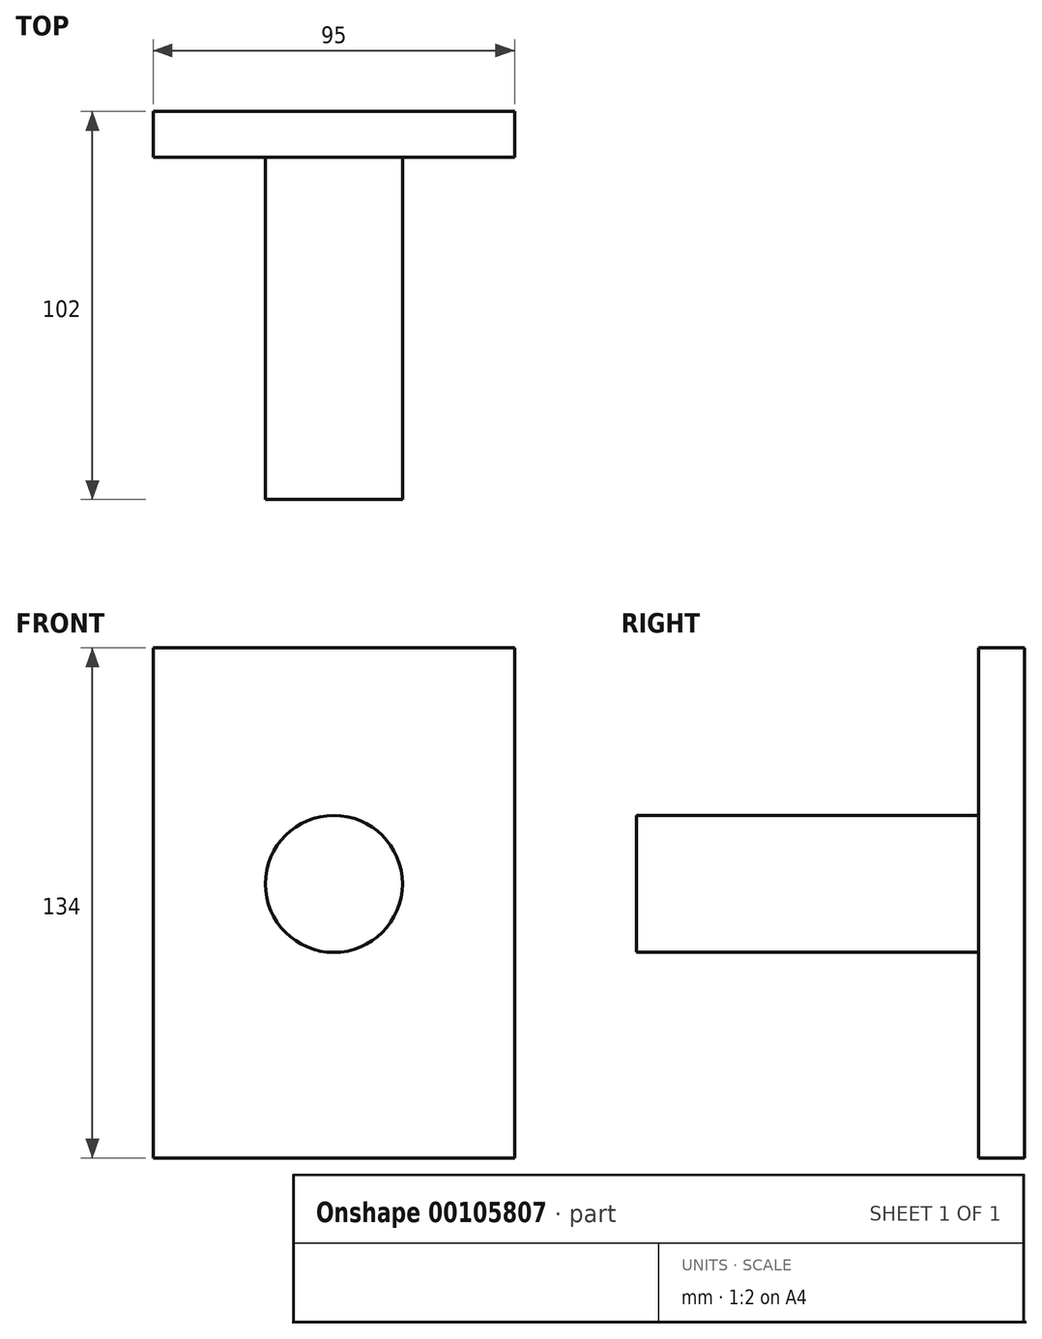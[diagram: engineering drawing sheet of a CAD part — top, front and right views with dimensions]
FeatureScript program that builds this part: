
annotation { "Feature Type Name" : "Feature", "Feature Type Description" : "" }
export const myFeature = defineFeature(function(context is Context, id is Id, definition is map)
    precondition{}
    {
        {
            var Q0;
            Q0=qCreatedBy(makeId("Front.planeOp"),FACE);
            var sketch = newSketch(context, id + "F0", { "sketchPlane" : qUnion([Q0])});
            skLineSegment(sketch, "E0", {"start": v(0, 0) * mm, "end": v(47.5, 0) * mm});
            skLineSegment(sketch, "E1", {"start": v(47.5, 0) * mm, "end": v(47.5, 67) * mm});
            skLineSegment(sketch, "E2", {"start": v(47.5, 67) * mm, "end": v(0, 67) * mm});
            skLineSegment(sketch, "E3.bottom", {"start": v(47.5, 67) * mm, "end": v(-47.5, 67) * mm});
            skLineSegment(sketch, "E3.top", {"start": v(47.5, -67) * mm, "end": v(-47.5, -67) * mm});
            skLineSegment(sketch, "E3.left", {"start": v(47.5, 67) * mm, "end": v(47.5, -67) * mm});
            skLineSegment(sketch, "E3.right", {"start": v(-47.5, 67) * mm, "end": v(-47.5, -67) * mm});
            skSolve(sketch);
        }
        {
            var Q0;
            Q0 = qSketchRegion(id + "F0", true);
            extrude(context, id + "F1", {"entities" : qUnion([Q0]), "depth" : 12 * mm});
        }
        {
            var Q0;
            Q0=makeQuery(id+"F1.opExtrude","CAP_FACE",FACE,{"disambiguationData":[OSD([sQuery(id+"F0.wireOp",EDGE,"E3.bottom"),sQuery(id+"F0.wireOp",EDGE,"E3.top"),sQuery(id+"F0.wireOp",EDGE,"E3.left"),sQuery(id+"F0.wireOp",EDGE,"E3.right")])],"isStart":false});
            var sketch = newSketch(context, id + "F2", { "sketchPlane" : qUnion([Q0])});
            skLineSegment(sketch, "E4", {"start": v(0, 0) * mm, "end": v(-20, 0) * mm});
            skLineSegment(sketch, "E5", {"start": v(-20, 0) * mm, "end": v(-20, -13) * mm});
            skCircle(sketch, "E6", {"center": v(-20, -13) * mm, "radius": 18 * mm});
            skCircle(sketch, "E7", {"center": v(-20, -13) * mm, "radius": 20 * mm});
            skLineSegment(sketch, "E8", {"start": v(0, 0) * mm, "end": v(0, 5) * mm});
            skCircle(sketch, "E9", {"center": v(0, 5) * mm, "radius": 18 * mm});
            skLineSegment(sketch, "E10", {"start": v(0, 0) * mm, "end": v(0, 23) * mm});
            skLineSegment(sketch, "E11", {"start": v(0, 23) * mm, "end": v(-15, 23) * mm});
            skCircle(sketch, "E12", {"center": v(-15, 23) * mm, "radius": 13 * mm});
            skCircle(sketch, "E13", {"center": v(-15, 23) * mm, "radius": 15 * mm});
            skSolve(sketch);
        }
        {
            var Q0;
            {var subQ0=sQuery(id+"F2.wireOp",EDGE,"E7");var subQ1=makeQuery(id+"F2.imprint","INTERSECT",VERTEX,{"derivedFrom":[sQuery(id+"F2.wireOp",EDGE,"E4"),subQ0]});Q0=makeQuery(id+"F2.imprint","IMPRINT",FACE,{"disambiguationData":[TD([[makeQuery(id+"F2.imprint","IMPRINT",EDGE,{"disambiguationData":[TD([[subQ1,1.0]])],"derivedFrom":subQ0}),-1.0]])]});}
            var Q1;
            {var subQ0=sQuery(id+"F2.wireOp",EDGE,"E9");var subQ1=sQuery(id+"F2.wireOp",EDGE,"E4");var subQ2=makeQuery(id+"F2.imprint","INTERSECT",VERTEX,{"derivedFrom":[subQ1,subQ0]});Q1=makeQuery(id+"F2.imprint","IMPRINT",FACE,{"disambiguationData":[TD([[makeQuery(id+"F2.imprint","IMPRINT",EDGE,{"disambiguationData":[TD([[subQ2,1.0]])],"derivedFrom":subQ1}),1.0]])]});}
            var Q2;
            {var subQ0=sQuery(id+"F2.wireOp",EDGE,"E9");var subQ1=sQuery(id+"F2.wireOp",EDGE,"E4");var subQ2=makeQuery(id+"F2.imprint","INTERSECT",VERTEX,{"derivedFrom":[subQ1,subQ0]});Q2=makeQuery(id+"F2.imprint","IMPRINT",FACE,{"disambiguationData":[TD([[makeQuery(id+"F2.imprint","IMPRINT",EDGE,{"disambiguationData":[TD([[subQ2,1.0]])],"derivedFrom":subQ1}),-1.0]])]});}
            var Q3;
            {var subQ0=sQuery(id+"F2.wireOp",EDGE,"E7");var subQ1=sQuery(id+"F2.wireOp",EDGE,"E4");var subQ2=makeQuery(id+"F2.imprint","INTERSECT",VERTEX,{"derivedFrom":[subQ1,subQ0]});Q3=makeQuery(id+"F2.imprint","IMPRINT",FACE,{"disambiguationData":[TD([[makeQuery(id+"F2.imprint","IMPRINT",EDGE,{"disambiguationData":[TD([[subQ2,-1.0]])],"derivedFrom":subQ1}),-1.0]])]});}
            var Q4;
            {var subQ0=sQuery(id+"F2.wireOp",EDGE,"E7");var subQ1=sQuery(id+"F2.wireOp",EDGE,"E4");var subQ2=makeQuery(id+"F2.imprint","INTERSECT",VERTEX,{"derivedFrom":[subQ1,subQ0]});Q4=makeQuery(id+"F2.imprint","IMPRINT",FACE,{"disambiguationData":[TD([[makeQuery(id+"F2.imprint","IMPRINT",EDGE,{"disambiguationData":[TD([[subQ2,-1.0]])],"derivedFrom":subQ1}),1.0]])]});}
            var Q5;
            {var subQ7=sQuery(id+"F2.wireOp",EDGE,"E10");var subQ9=makeQuery(id+"F2.imprint","IMPRINT",VERTEX,{"derivedFrom":subQ7});Q5=makeQuery(id+"F2.imprint","IMPRINT",FACE,{"disambiguationData":[TD([[makeQuery(id+"F2.imprint","IMPRINT",EDGE,{"disambiguationData":[TD([[subQ9,1.0]])],"derivedFrom":subQ7}),1.0]])]});}
            var Q6;
            {var subQ1=sQuery(id+"F2.wireOp",EDGE,"E9");var subQ3=sQuery(id+"F2.wireOp",EDGE,"E12");var subQ5=makeQuery(id+"F2.imprint","INTERSECT",VERTEX,{"disambiguationData":[OD(1.0)],"derivedFrom":[subQ1,subQ3]});Q6=makeQuery(id+"F2.imprint","IMPRINT",FACE,{"disambiguationData":[TD([[makeQuery(id+"F2.imprint","IMPRINT",EDGE,{"disambiguationData":[TD([[subQ5,-1.0]])],"derivedFrom":subQ1}),1.0]])]});}
            var Q7;
            {var subQ0=sQuery(id+"F2.wireOp",EDGE,"E12");var subQ1=sQuery(id+"F2.wireOp",EDGE,"E9");var subQ2=makeQuery(id+"F2.imprint","INTERSECT",VERTEX,{"disambiguationData":[OD(0.0)],"derivedFrom":[subQ1,subQ0]});Q7=makeQuery(id+"F2.imprint","IMPRINT",FACE,{"disambiguationData":[TD([[makeQuery(id+"F2.imprint","IMPRINT",EDGE,{"disambiguationData":[TD([[subQ2,-1.0]])],"derivedFrom":subQ1}),1.0]])]});}
            extrude(context, id + "F3", {"entities" : qUnion([Q0, Q1, Q2, Q3, Q4, Q5, Q6, Q7]), "operationType" : NewBodyOperationType.ADD, "depth" : 90 * mm});
        }
        {
            var Q0;
            Q0=makeQuery(id+"F2.imprint","IMPRINT",FACE,{"disambiguationData":[TD([[makeQuery(id+"F2.imprint","IMPRINT",EDGE,{"derivedFrom":makeQuery(id+"F1.opExtrude","CAP_EDGE",EDGE,{"disambiguationData":[OSD([sQuery(id+"F0.wireOp",EDGE,"E3.bottom")])],"isStart":false})}),1.0]])]});
            var sketch = newSketch(context, id + "F4", { "sketchPlane" : qUnion([Q0])});
            skLineSegment(sketch, "E14", {"start": v(0, 0) * mm, "end": v(0, 67) * mm});
            skLineSegment(sketch, "E15", {"start": v(0, 67) * mm, "end": v(0, 72) * mm});
            skLineSegment(sketch, "E16", {"start": v(0, 72) * mm, "end": v(-60.28, 72) * mm});
            skLineSegment(sketch, "E17", {"start": v(-60.28, 72) * mm, "end": v(75.95, 72) * mm});
            skLineSegment(sketch, "E18", {"start": v(0, 0) * mm, "end": v(3.42, 0) * mm});
            skLineSegment(sketch, "E19.MirrorCS", {"start": v(-60.28, -72) * mm, "end": v(75.95, -72) * mm});
            skSolve(sketch);
        }
        {
            var Q0;
            Q0=makeQuery(id+"F1.opExtrude","SWEPT_FACE",FACE,{"disambiguationData":[OSD([sQuery(id+"F0.wireOp",EDGE,"E3.top")])]});
            var Q1;
            Q1=sQuery(id+"F4.wireOp",EDGE,"E19.MirrorCS");
            cPlane(context, id + "F5", {"entities" : qUnion([Q0, Q1]), "cplaneType" : CPlaneType.LINE_ANGLE, "offset" : 25 * mm, "angle" : 10 * degree, "width" : 150 * mm, "height" : 150 * mm});
        }
    });
